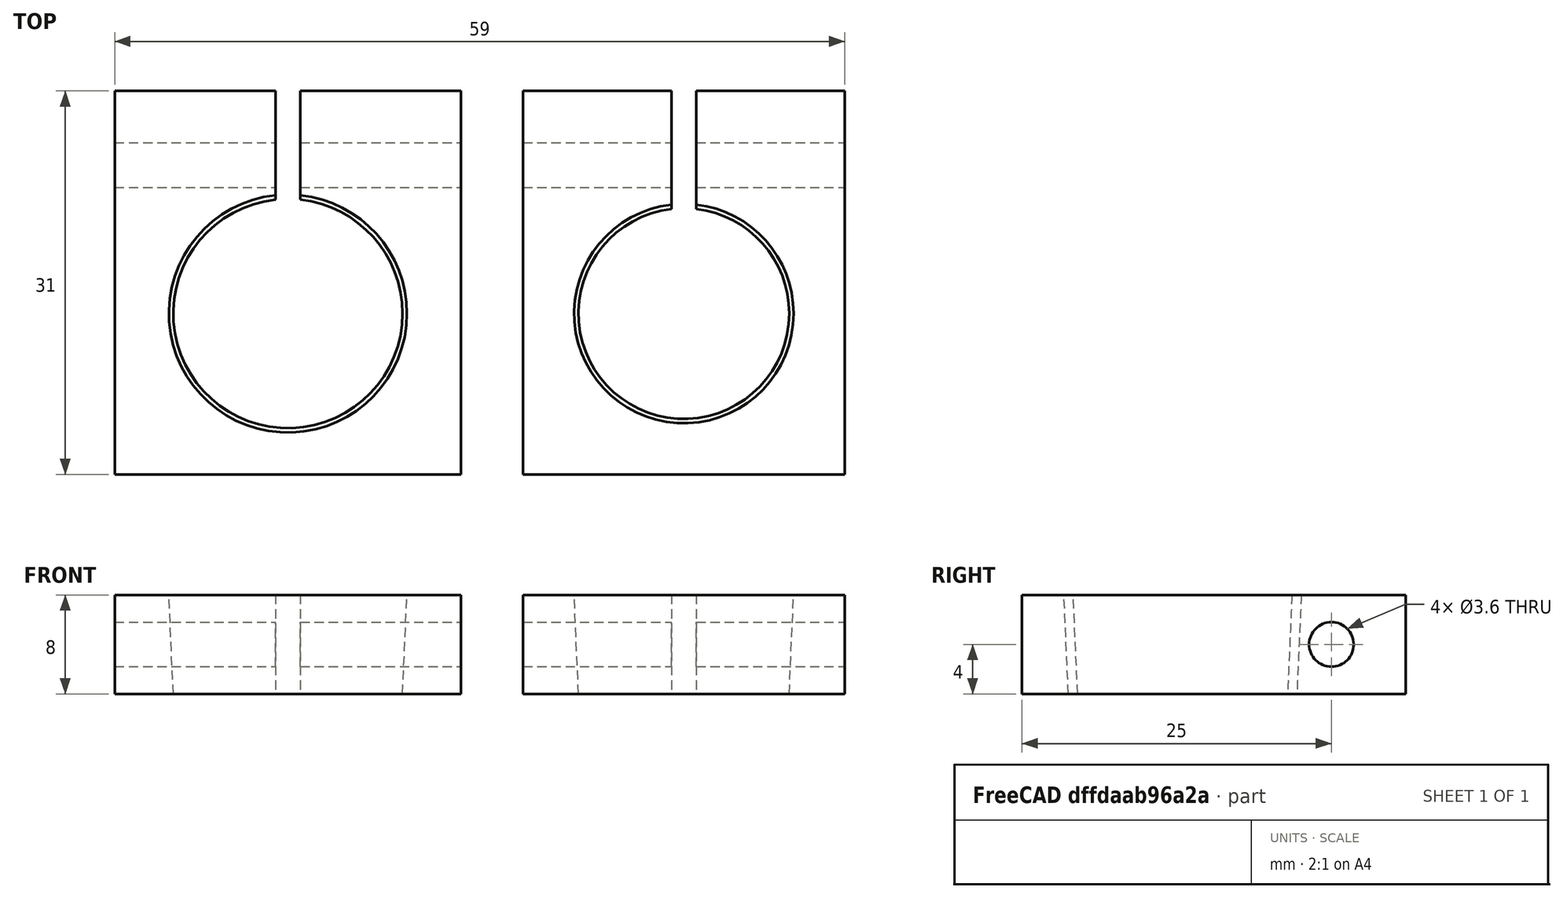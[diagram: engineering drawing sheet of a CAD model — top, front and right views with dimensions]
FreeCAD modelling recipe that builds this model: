
FCSTD DOCUMENT  (FreeCAD 0.14R3702 (Git))
Label: batt-clamp
License: CC-BY 3.0
LicenseURL: http://creativecommons.org/licenses/by/3.0/
objects: Part::Cut×6, Part::Box×4, Part::Cone×2, Part::Cylinder×2
note: 14 computed .brp shape members not serialized (recipe doc carries the construction recipe); baked Part::Feature solids carry a one-line shape summary decoded from their .brp

FEATURE [Part::Cone] Cone  label="cone-pos"
  Angle = 360
  Height = 17
  Radius1 = 9
  Radius2 = 9.75
FEATURE [Part::Box] Box  label="Cube"
  Height = 8
  Length = 26
  Placement = pos=(-13,-13,6) rot=(0,0,1;0rad)
  Width = 31
FEATURE [Part::Cylinder] Cylinder
  Angle = 360
  Height = 43
  Placement = pos=(-23,12,10) rot=(0,1,0;1.5708rad)
  Radius = 1.8
FEATURE [Part::Box] Box002  label="Cube002"
  Height = 19
  Length = 2
  Placement = pos=(-1,0,0) rot=(0,0,1;0rad)
  Width = 29
FEATURE [Part::Cone] Cone001  label="cone-neg"
  Angle = 360
  Height = 17
  Radius1 = 8.25
  Radius2 = 9
FEATURE [Part::Box] Box004  label="Cube004"
  Height = 19
  Length = 2
  Placement = pos=(-1,0,0) rot=(0,0,1;0rad)
  Width = 29
FEATURE [Part::Box] Box005  label="Cube005"
  Height = 8
  Length = 28
  Placement = pos=(-14,-13,6) rot=(0,0,1;0rad)
  Width = 31
FEATURE [Part::Cylinder] Cylinder001
  Angle = 360
  Height = 43
  Placement = pos=(-23,12,10) rot=(0,1,0;1.5708rad)
  Radius = 1.8
FEATURE [Part::Cut] Cut
  Base = -> Box
  Tool = -> Cone001
FEATURE [Part::Cut] Cut001
  Base = -> Cut
  Tool = -> Cylinder
FEATURE [Part::Cut] Cut002  label="clamp-neg"
  Base = -> Cut001
  Placement = pos=(32,0,0) rot=(0,0,1;0rad)
  Tool = -> Box002
FEATURE [Part::Cut] Cut003
  Base = -> Box005
  Tool = -> Cone
FEATURE [Part::Cut] Cut004
  Base = -> Cut003
  Tool = -> Cylinder001
FEATURE [Part::Cut] Cut005  label="clamp-pos"
  Base = -> Cut004
  Tool = -> Box004
